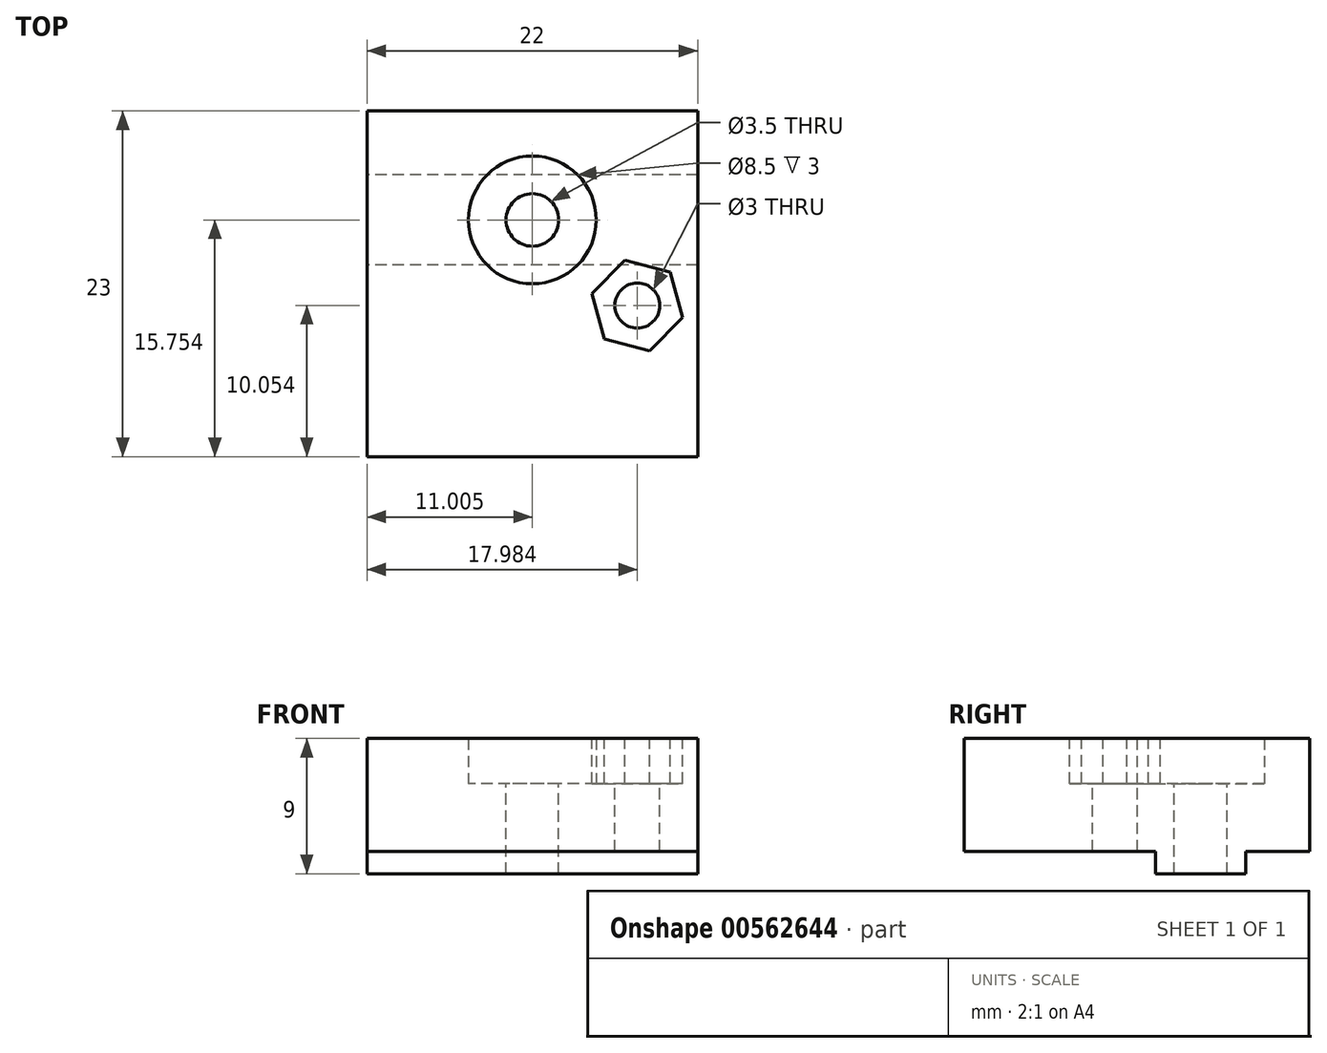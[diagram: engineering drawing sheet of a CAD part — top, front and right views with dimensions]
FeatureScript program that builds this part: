
annotation { "Feature Type Name" : "Feature", "Feature Type Description" : "" }
export const myFeature = defineFeature(function(context is Context, id is Id, definition is map)
    precondition{}
    {
        {
            var Q0;
            Q0=qCreatedBy(makeId("Top.planeOp"),FACE);
            var sketch = newSketch(context, id + "F0", { "sketchPlane" : qUnion([Q0])});
            skLineSegment(sketch, "E0.bottom", {"start": v(-9.07, 8.56) * mm, "end": v(12.93, 8.56) * mm});
            skLineSegment(sketch, "E0.top", {"start": v(-9.07, -14.44) * mm, "end": v(12.93, -14.44) * mm});
            skLineSegment(sketch, "E0.left", {"start": v(-9.07, 8.56) * mm, "end": v(-9.07, -14.44) * mm});
            skLineSegment(sketch, "E0.right", {"start": v(12.93, 8.56) * mm, "end": v(12.93, -14.44) * mm});
            skSolve(sketch);
        }
        {
            var Q0;
            Q0=makeQuery(id+"F0.imprint","IMPRINT",FACE,{"disambiguationData":[TD([[makeQuery(id+"F0.imprint","IMPRINT",EDGE,{"derivedFrom":sQuery(id+"F0.wireOp",EDGE,"E0.bottom")}),-1.0]])]});
            extrude(context, id + "F1", {"entities" : qUnion([Q0]), "depth" : 4.5 * mm, "offsetDistance" : 25 * mm});
        }
        {
            var Q0;
            Q0=makeQuery(id+"F1.opExtrude","CAP_FACE",FACE,{"disambiguationData":[OSD([sQuery(id+"F0.wireOp",EDGE,"E0.bottom"),sQuery(id+"F0.wireOp",EDGE,"E0.top"),sQuery(id+"F0.wireOp",EDGE,"E0.left"),sQuery(id+"F0.wireOp",EDGE,"E0.right")])],"isStart":false});
            var sketch = newSketch(context, id + "F2", { "sketchPlane" : qUnion([Q0])});
            skCircle(sketch, "E1", {"center": v(1.93, 1.31) * mm, "radius": 4.25 * mm});
            skPoint(sketch, "E1.centerSnap0", {"position": v(1.93, 8.56) * mm});
            skCircle(sketch, "E2", {"center": v(1.93, 1.31) * mm, "radius": 1.75 * mm});
            skPoint(sketch, "E3", {"position": v(12.93, -1.44) * mm});
            skPoint(sketch, "E4", {"position": v(-9.07, -10.44) * mm});
            skCircle(sketch, "E5.cCircle", {"center": v(-5.04, -4.39) * mm, "radius": 2.7 * mm, "construction": true});
            skLineSegment(sketch, "E5.0", {"start": v(-8.06, -5.17) * mm, "end": v(-7.24, -2.17) * mm});
            skLineSegment(sketch, "E5.1", {"start": v(-7.24, -2.17) * mm, "end": v(-4.22, -1.38) * mm});
            skLineSegment(sketch, "E5.2", {"start": v(-4.22, -1.38) * mm, "end": v(-2.03, -3.6) * mm});
            skLineSegment(sketch, "E5.3", {"start": v(-2.03, -3.6) * mm, "end": v(-2.85, -6.6) * mm});
            skLineSegment(sketch, "E5.4", {"start": v(-2.85, -6.6) * mm, "end": v(-5.87, -7.4) * mm});
            skLineSegment(sketch, "E5.5", {"start": v(-5.87, -7.4) * mm, "end": v(-8.06, -5.17) * mm});
            skPoint(sketch, "E5.0.midPoint", {"position": v(-7.65, -3.67) * mm});
            skCircle(sketch, "E6", {"center": v(-5.04, -4.39) * mm, "radius": 1.5 * mm});
            skSolve(sketch);
        }
        {
            var Q0;
            Q0=makeQuery(id+"F2.imprint","IMPRINT",FACE,{"disambiguationData":[TD([[makeQuery(id+"F2.imprint","IMPRINT",EDGE,{"derivedFrom":sQuery(id+"F2.wireOp",EDGE,"E2")}),1.0]])]});
            extrude(context, id + "F3", {"entities" : qUnion([Q0]), "operationType" : NewBodyOperationType.REMOVE, "endBound" : BoundingType.THROUGH_ALL, "oppositeDirection" : true, "depth" : 25 * mm, "offsetDistance" : 25 * mm});
        }
        {
            var Q0;
            Q0=makeQuery(id+"F1.opExtrude","CAP_FACE",FACE,{"disambiguationData":[OSD([sQuery(id+"F0.wireOp",EDGE,"E0.bottom"),sQuery(id+"F0.wireOp",EDGE,"E0.top"),sQuery(id+"F0.wireOp",EDGE,"E0.left"),sQuery(id+"F0.wireOp",EDGE,"E0.right")])],"isStart":true});
            var sketch = newSketch(context, id + "F4", { "sketchPlane" : qUnion([Q0])});
            skLineSegment(sketch, "E7.bottom", {"start": v(12.93, -4.31) * mm, "end": v(-9.07, -4.31) * mm});
            skLineSegment(sketch, "E7.top", {"start": v(12.93, 1.69) * mm, "end": v(-9.07, 1.69) * mm});
            skLineSegment(sketch, "E7.left", {"start": v(12.93, -4.31) * mm, "end": v(12.93, 1.69) * mm});
            skLineSegment(sketch, "E7.right", {"start": v(-9.07, -4.31) * mm, "end": v(-9.07, 1.69) * mm});
            skPoint(sketch, "E7.middle", {"position": v(1.93, -1.31) * mm});
            skSolve(sketch);
        }
        {
            var Q0;
            Q0=makeQuery(id+"F4.imprint","IMPRINT",FACE,{"disambiguationData":[TD([[makeQuery(id+"F4.imprint","IMPRINT",EDGE,{"derivedFrom":sQuery(id+"F4.wireOp",EDGE,"E7.bottom")}),-1.0]])]});
            extrude(context, id + "F5", {"entities" : qUnion([Q0]), "operationType" : NewBodyOperationType.ADD, "depth" : 1.5 * mm, "offsetDistance" : 25 * mm});
        }
        {
            var Q0;
            Q0=makeQuery(id+"F2.imprint","IMPRINT",FACE,{"disambiguationData":[TD([[makeQuery(id+"F2.imprint","IMPRINT",EDGE,{"derivedFrom":sQuery(id+"F2.wireOp",EDGE,"E1")}),-1.0]])]});
            var Q1;
            Q1=makeQuery(id+"F2.imprint","IMPRINT",FACE,{"disambiguationData":[TD([[makeQuery(id+"F2.imprint","IMPRINT",EDGE,{"derivedFrom":sQuery(id+"F2.wireOp",EDGE,"E5.0")}),-1.0]])]});
            var Q2;
            Q2=makeQuery(id+"F2.imprint","IMPRINT",FACE,{"disambiguationData":[TD([[makeQuery(id+"F2.imprint","IMPRINT",EDGE,{"derivedFrom":sQuery(id+"F2.wireOp",EDGE,"E6")}),1.0]])]});
            extrude(context, id + "F6", {"entities" : qUnion([Q0, Q1, Q2]), "operationType" : NewBodyOperationType.ADD, "depth" : 3 * mm, "offsetDistance" : 25 * mm});
        }
        {
            var Q0;
            Q0=makeQuery(id+"F6.opExtrude","CAP_FACE",FACE,{"disambiguationData":[OSD([sQuery(id+"F0.wireOp",EDGE,"E0.bottom"),sQuery(id+"F0.wireOp",EDGE,"E0.top"),sQuery(id+"F0.wireOp",EDGE,"E0.left"),sQuery(id+"F0.wireOp",EDGE,"E0.right"),sQuery(id+"F2.wireOp",EDGE,"E1")])],"isStart":false});
            var sketch = newSketch(context, id + "F7", { "sketchPlane" : qUnion([Q0])});
            skLineSegment(sketch, "E8.0", {"start": v(-4.22, -1.38) * mm, "end": v(-2.03, -3.6) * mm});
            skLineSegment(sketch, "E9.0", {"start": v(-7.24, -2.17) * mm, "end": v(-4.22, -1.38) * mm});
            skLineSegment(sketch, "E10.0", {"start": v(-8.06, -5.17) * mm, "end": v(-7.24, -2.17) * mm});
            skLineSegment(sketch, "E11.0", {"start": v(-5.87, -7.4) * mm, "end": v(-8.06, -5.17) * mm});
            skLineSegment(sketch, "E12.0", {"start": v(-2.85, -6.6) * mm, "end": v(-5.87, -7.4) * mm});
            skLineSegment(sketch, "E13.0", {"start": v(-2.03, -3.6) * mm, "end": v(-2.85, -6.6) * mm});
            skCircle(sketch, "E14.0", {"center": v(-5.04, -4.39) * mm, "radius": 1.5 * mm});
            skLineSegment(sketch, "E15", {"start": v(1.93, 8.56) * mm, "end": v(1.93, -14.44) * mm, "construction": true});
            skLineSegment(sketch, "E16.MirrorCS", {"start": v(5.9, -3.6) * mm, "end": v(6.72, -6.6) * mm});
            skLineSegment(sketch, "E17.MirrorCS", {"start": v(8.09, -1.38) * mm, "end": v(5.9, -3.6) * mm});
            skLineSegment(sketch, "E18.MirrorCS", {"start": v(11.1, -2.17) * mm, "end": v(8.09, -1.38) * mm});
            skLineSegment(sketch, "E19.MirrorCS", {"start": v(11.93, -5.17) * mm, "end": v(11.1, -2.17) * mm});
            skLineSegment(sketch, "E20.MirrorCS", {"start": v(9.74, -7.4) * mm, "end": v(11.93, -5.17) * mm});
            skLineSegment(sketch, "E21.MirrorCS", {"start": v(6.72, -6.6) * mm, "end": v(9.74, -7.4) * mm});
            skCircle(sketch, "E22.MirrorC", {"center": v(8.91, -4.39) * mm, "radius": 1.5 * mm});
            skSolve(sketch);
        }
        {
            var Q0;
            Q0=makeQuery(id+"F7.imprint","IMPRINT",FACE,{"disambiguationData":[TD([[makeQuery(id+"F7.imprint","IMPRINT",EDGE,{"derivedFrom":sQuery(id+"F7.wireOp",EDGE,"E17.MirrorCS")}),1.0]])]});
            extrude(context, id + "F8", {"entities" : qUnion([Q0]), "operationType" : NewBodyOperationType.REMOVE, "oppositeDirection" : true, "depth" : 3 * mm, "offsetDistance" : 25 * mm});
        }
        {
            var Q0;
            Q0=makeQuery(id+"F8.boolean.opBoolean","SPLIT",FACE,{"disambiguationData":[TD([makeQuery(id+"F8.opExtrude","SWEPT_FACE",FACE,{"disambiguationData":[OSD([sQuery(id+"F7.wireOp",EDGE,"E22.MirrorC")])]})])],"derivedFrom":makeQuery(id+"F6.opExtrude","CAP_FACE",FACE,{"disambiguationData":[OSD([sQuery(id+"F0.wireOp",EDGE,"E0.bottom"),sQuery(id+"F0.wireOp",EDGE,"E0.top"),sQuery(id+"F0.wireOp",EDGE,"E0.left"),sQuery(id+"F0.wireOp",EDGE,"E0.right"),sQuery(id+"F2.wireOp",EDGE,"E1")])],"isStart":false})});
            extrude(context, id + "F9", {"entities" : qUnion([Q0]), "operationType" : NewBodyOperationType.REMOVE, "endBound" : BoundingType.THROUGH_ALL, "oppositeDirection" : true, "depth" : 25 * mm, "offsetDistance" : 25 * mm});
        }
    });
